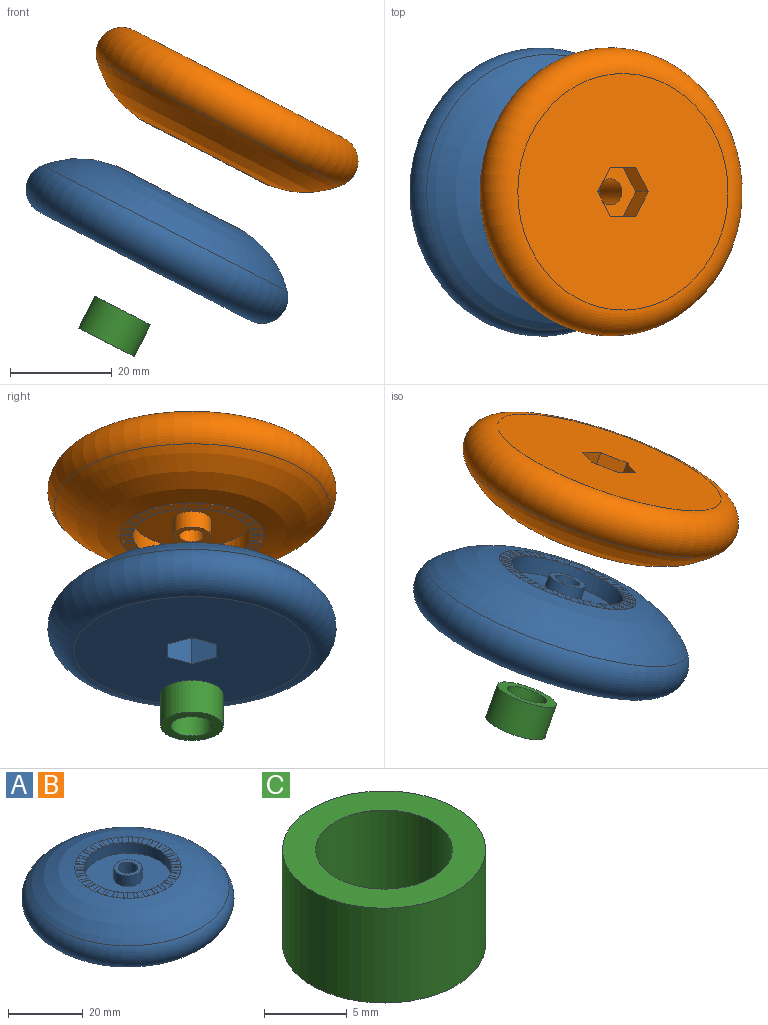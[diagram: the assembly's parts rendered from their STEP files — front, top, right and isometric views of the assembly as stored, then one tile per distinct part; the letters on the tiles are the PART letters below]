
ASSEMBLY  parts=3 mates=2
PART A: 166 faces, bbox 61.3x61.3x15 mm
  f0: plane 46.41x46.41mm, normal (0,0,-1), area 1611mm2, adj f7,f8,f9,f10,f11,f12,f13
  f1: plane 7.5x7.5mm, normal (0,0,1), area 23.7mm2, adj f6,f15
  f2: revolved ~53.87x53.87mm, area 3890.3mm2, adj f3,f7,f17,f22,f27,f32,f37,f42
  f3: plane 28.34x28.32mm, normal (0,0,1), area 130mm2, adj f2,f4,f16,f18,f19,f21,f23,f24
  f4: cylinder r=11.62mm len=23.25mm, axis (0,0,-1), area 255.6mm2, adj f3,f5
  f5: plane 23.25x23.25mm, normal (0,0,1), area 380.4mm2, adj f4,f6
  f6: cylinder r=3.75mm len=7.5mm, axis (0,0,-1), area 82.5mm2, adj f1,f5
  f7: torus R=23.21mm, axis (0,0,-1), area 1972.1mm2, adj f0,f2
  f8: plane 5.42x4.83mm, normal (-0.87,0.5,0), area 30.2mm2, adj f0,f9,f13,f14
  f9: plane 5.58x5.42mm, normal (0,1,0), area 30.2mm2, adj f0,f8,f10,f14
  f10: plane 5.42x4.83mm, normal (0.87,0.5,0), area 30.2mm2, adj f0,f9,f11,f14
  f11: plane 5.42x4.83mm, normal (0.87,-0.5,0), area 30.2mm2, adj f0,f10,f12,f14
  f12: plane 5.58x5.42mm, normal (0,-1,0), area 30.2mm2, adj f0,f11,f13,f14
  f13: plane 5.42x4.83mm, normal (-0.87,-0.5,0), area 30.2mm2, adj f0,f8,f12,f14
  f14: plane 11.16x9.66mm, normal (0,0,-1), area 60.4mm2, adj f8,f9,f10,f11,f12,f13,f15
  f15: cylinder r=2.55mm len=9.48mm, axis (0,0,1), area 152.1mm2, adj f1,f14
  f16: plane 2.52x0.1mm, normal (1,0,0), area 0.3mm2, adj f3,f17,f19,f20
  f17: plane 1.02x0.12mm, normal (0,1,0), area 0.1mm2, adj f2,f16,f18,f20
  f18: plane 2.52x0.1mm, normal (-1,0,0), area 0.3mm2, adj f3,f17,f19,f20
  f19: plane 1x0.1mm, normal (0,-1,0), area 0.1mm2, adj f3,f16,f18,f20
  f20: plane 2.52x1mm, normal (0,0,1), area 2.5mm2, adj f16,f17,f18,f19
  f21: plane 2.47x0.52mm, normal (0.98,-0.21,0), area 0.3mm2, adj f3,f22,f24,f25
  f22: plane 1x0.23mm, normal (0.21,0.98,0), area 0.1mm2, adj f2,f21,f23,f25
  f23: plane 2.47x0.52mm, normal (-0.98,0.21,0), area 0.3mm2, adj f3,f22,f24,f25
  f24: plane 0.98x0.21mm, normal (-0.21,-0.98,0), area 0.1mm2, adj f3,f21,f23,f25
  f25: plane 2.68x1.5mm, normal (0,0,1), area 2.5mm2, adj f21,f22,f23,f24
  f26: plane 2.3x1.03mm, normal (0.91,-0.41,0), area 0.3mm2, adj f3,f27,f29,f30
  f27: plane 0.93x0.42mm, normal (0.41,0.91,0), area 0.1mm2, adj f2,f26,f28,f30
  f28: plane 2.3x1.03mm, normal (-0.91,0.41,0), area 0.3mm2, adj f3,f27,f29,f30
  f29: plane 0.91x0.41mm, normal (-0.41,-0.91,0), area 0.1mm2, adj f3,f26,f28,f30
  f30: plane 2.71x1.94mm, normal (0,0,1), area 2.5mm2, adj f26,f27,f28,f29
  f31: plane 2.04x1.48mm, normal (0.81,-0.59,0), area 0.3mm2, adj f3,f32,f34,f35
  f32: plane 0.83x0.61mm, normal (0.59,0.81,0), area 0.1mm2, adj f2,f31,f33,f35
  f33: plane 2.04x1.48mm, normal (-0.81,0.59,0), area 0.3mm2, adj f3,f32,f34,f35
  f34: plane 0.81x0.59mm, normal (-0.59,-0.81,0), area 0.1mm2, adj f3,f31,f33,f35
  f35: plane 2.63x2.29mm, normal (0,0,1), area 2.5mm2, adj f31,f32,f33,f34
  f36: plane 1.88x1.69mm, normal (0.67,-0.74,0), area 0.3mm2, adj f3,f37,f39,f40
  f37: plane 0.76x0.69mm, normal (0.74,0.67,0), area 0.1mm2, adj f2,f36,f38,f40
  f38: plane 1.87x1.69mm, normal (-0.67,0.74,0), area 0.3mm2, adj f3,f37,f39,f40
  f39: plane 0.74x0.67mm, normal (-0.74,-0.67,0), area 0.1mm2, adj f3,f36,f38,f40
  f40: plane 2.54x2.43mm, normal (0,0,1), area 2.5mm2, adj f36,f37,f38,f39
  f41: plane 2.19x1.26mm, normal (0.5,-0.87,0), area 0.3mm2, adj f3,f42,f44,f45
  f42: plane 0.88x0.52mm, normal (0.87,0.5,0), area 0.1mm2, adj f2,f41,f43,f45
  f43: plane 2.19x1.26mm, normal (-0.5,0.87,0), area 0.3mm2, adj f3,f42,f44,f45
  f44: plane 0.87x0.5mm, normal (-0.87,-0.5,0), area 0.1mm2, adj f3,f41,f43,f45
  f45: plane 2.68x2.13mm, normal (0,0,1), area 2.5mm2, adj f41,f42,f43,f44
  f46: plane 2.4x0.78mm, normal (0.31,-0.95,0), area 0.3mm2, adj f3,f47,f49,f50
  f47: plane 0.97x0.33mm, normal (0.95,0.31,0), area 0.1mm2, adj f2,f46,f48,f50
  f48: plane 2.4x0.78mm, normal (-0.31,0.95,0), area 0.3mm2, adj f3,f47,f49,f50
  f49: plane 0.95x0.31mm, normal (-0.95,-0.31,0), area 0.1mm2, adj f3,f46,f48,f50
  f50: plane 2.71x1.73mm, normal (0,0,1), area 2.5mm2, adj f46,f47,f48,f49
  f51: plane 2.51x0.26mm, normal (0.1,-0.99,0), area 0.3mm2, adj f3,f52,f54,f55
  f52: plane 1.01x0.12mm, normal (0.99,0.1,0), area 0.1mm2, adj f2,f51,f53,f55
  f53: plane 2.51x0.26mm, normal (-0.1,0.99,0), area 0.3mm2, adj f3,f52,f54,f55
  f54: plane 0.99x0.1mm, normal (-0.99,-0.1,0), area 0.1mm2, adj f3,f51,f53,f55
  f55: plane 2.61x1.26mm, normal (0,0,1), area 2.5mm2, adj f51,f52,f53,f54
  f56: plane 2.51x0.26mm, normal (-0.1,-0.99,0), area 0.3mm2, adj f3,f57,f59,f60
  f57: plane 1.01x0.12mm, normal (0.99,-0.1,0), area 0.1mm2, adj f2,f56,f58,f60
  f58: plane 2.51x0.26mm, normal (0.1,0.99,0), area 0.3mm2, adj f3,f57,f59,f60
  f59: plane 0.99x0.1mm, normal (-0.99,0.1,0), area 0.1mm2, adj f3,f56,f58,f60
  f60: plane 2.61x1.26mm, normal (0,0,1), area 2.5mm2, adj f56,f57,f58,f59
  f61: plane 2.4x0.78mm, normal (-0.31,-0.95,0), area 0.3mm2, adj f3,f62,f64,f65
  f62: plane 0.97x0.33mm, normal (0.95,-0.31,0), area 0.1mm2, adj f2,f61,f63,f65
  f63: plane 2.4x0.78mm, normal (0.31,0.95,0), area 0.3mm2, adj f3,f62,f64,f65
  f64: plane 0.95x0.31mm, normal (-0.95,0.31,0), area 0.1mm2, adj f3,f61,f63,f65
  f65: plane 2.71x1.73mm, normal (0,0,1), area 2.5mm2, adj f61,f62,f63,f64
  f66: plane 2.19x1.26mm, normal (-0.5,-0.87,0), area 0.3mm2, adj f3,f67,f69,f70
  f67: plane 0.88x0.52mm, normal (0.87,-0.5,0), area 0.1mm2, adj f2,f66,f68,f70
  f68: plane 2.19x1.26mm, normal (0.5,0.87,0), area 0.3mm2, adj f3,f67,f69,f70
  f69: plane 0.87x0.5mm, normal (-0.87,0.5,0), area 0.1mm2, adj f3,f66,f68,f70
  f70: plane 2.68x2.13mm, normal (0,0,1), area 2.5mm2, adj f66,f67,f68,f69
  f71: plane 1.87x1.69mm, normal (-0.67,-0.74,0), area 0.3mm2, adj f3,f72,f74,f75
  f72: plane 0.76x0.69mm, normal (0.74,-0.67,0), area 0.1mm2, adj f2,f71,f73,f75
  f73: plane 1.88x1.69mm, normal (0.67,0.74,0), area 0.3mm2, adj f3,f72,f74,f75
  f74: plane 0.74x0.67mm, normal (-0.74,0.67,0), area 0.1mm2, adj f3,f71,f73,f75
  f75: plane 2.54x2.43mm, normal (0,0,1), area 2.5mm2, adj f71,f72,f73,f74
  f76: plane 2.04x1.48mm, normal (-0.81,-0.59,0), area 0.3mm2, adj f3,f77,f79,f80
  f77: plane 0.83x0.61mm, normal (0.59,-0.81,0), area 0.1mm2, adj f2,f76,f78,f80
  f78: plane 2.04x1.48mm, normal (0.81,0.59,0), area 0.3mm2, adj f3,f77,f79,f80
  f79: plane 0.81x0.59mm, normal (-0.59,0.81,0), area 0.1mm2, adj f3,f76,f78,f80
  f80: plane 2.63x2.29mm, normal (0,0,1), area 2.5mm2, adj f76,f77,f78,f79
  f81: plane 2.3x1.03mm, normal (-0.91,-0.41,0), area 0.3mm2, adj f3,f82,f84,f85
  f82: plane 0.93x0.42mm, normal (0.41,-0.91,0), area 0.1mm2, adj f2,f81,f83,f85
  f83: plane 2.3x1.03mm, normal (0.91,0.41,0), area 0.3mm2, adj f3,f82,f84,f85
  f84: plane 0.91x0.41mm, normal (-0.41,0.91,0), area 0.1mm2, adj f3,f81,f83,f85
  f85: plane 2.71x1.94mm, normal (0,0,1), area 2.5mm2, adj f81,f82,f83,f84
  f86: plane 2.47x0.52mm, normal (-0.98,-0.21,0), area 0.3mm2, adj f3,f87,f89,f90
  f87: plane 1x0.23mm, normal (0.21,-0.98,0), area 0.1mm2, adj f2,f86,f88,f90
  f88: plane 2.47x0.52mm, normal (0.98,0.21,0), area 0.3mm2, adj f3,f87,f89,f90
  f89: plane 0.98x0.21mm, normal (-0.21,0.98,0), area 0.1mm2, adj f3,f86,f88,f90
  f90: plane 2.68x1.5mm, normal (0,0,1), area 2.5mm2, adj f86,f87,f88,f89
  f91: plane 2.52x0.1mm, normal (-1,0,0), area 0.3mm2, adj f3,f92,f94,f95
  f92: plane 1.02x0.12mm, normal (0,-1,0), area 0.1mm2, adj f2,f91,f93,f95
  f93: plane 2.52x0.1mm, normal (1,0,0), area 0.3mm2, adj f3,f92,f94,f95
  f94: plane 1x0.1mm, normal (0,1,0), area 0.1mm2, adj f3,f91,f93,f95
  f95: plane 2.52x1mm, normal (0,0,1), area 2.5mm2, adj f91,f92,f93,f94
  f96: plane 2.47x0.52mm, normal (-0.98,0.21,0), area 0.3mm2, adj f3,f97,f99,f100
  f97: plane 1x0.23mm, normal (-0.21,-0.98,0), area 0.1mm2, adj f2,f96,f98,f100
  f98: plane 2.47x0.52mm, normal (0.98,-0.21,0), area 0.3mm2, adj f3,f97,f99,f100
  f99: plane 0.98x0.21mm, normal (0.21,0.98,0), area 0.1mm2, adj f3,f96,f98,f100
  f100: plane 2.68x1.5mm, normal (0,0,1), area 2.5mm2, adj f96,f97,f98,f99
  f101: plane 2.3x1.03mm, normal (-0.91,0.41,0), area 0.3mm2, adj f3,f102,f104,f105
  f102: plane 0.93x0.42mm, normal (-0.41,-0.91,0), area 0.1mm2, adj f2,f101,f103,f105
  f103: plane 2.3x1.03mm, normal (0.91,-0.41,0), area 0.3mm2, adj f3,f102,f104,f105
  f104: plane 0.91x0.41mm, normal (0.41,0.91,0), area 0.1mm2, adj f3,f101,f103,f105
  f105: plane 2.71x1.94mm, normal (0,0,1), area 2.5mm2, adj f101,f102,f103,f104
  f106: plane 2.04x1.48mm, normal (-0.81,0.59,0), area 0.3mm2, adj f3,f107,f109,f110
  f107: plane 0.83x0.61mm, normal (-0.59,-0.81,0), area 0.1mm2, adj f2,f106,f108,f110
  f108: plane 2.04x1.48mm, normal (0.81,-0.59,0), area 0.3mm2, adj f3,f107,f109,f110
  f109: plane 0.81x0.59mm, normal (0.59,0.81,0), area 0.1mm2, adj f3,f106,f108,f110
  f110: plane 2.63x2.29mm, normal (0,0,1), area 2.5mm2, adj f106,f107,f108,f109
  f111: plane 1.88x1.69mm, normal (-0.67,0.74,0), area 0.3mm2, adj f3,f112,f114,f115
  f112: plane 0.76x0.69mm, normal (-0.74,-0.67,0), area 0.1mm2, adj f2,f111,f113,f115
  f113: plane 1.87x1.69mm, normal (0.67,-0.74,0), area 0.3mm2, adj f3,f112,f114,f115
  f114: plane 0.74x0.67mm, normal (0.74,0.67,0), area 0.1mm2, adj f3,f111,f113,f115
  f115: plane 2.54x2.43mm, normal (0,0,1), area 2.5mm2, adj f111,f112,f113,f114
  f116: plane 2.19x1.26mm, normal (-0.5,0.87,0), area 0.3mm2, adj f3,f117,f119,f120
  f117: plane 0.88x0.52mm, normal (-0.87,-0.5,0), area 0.1mm2, adj f2,f116,f118,f120
  f118: plane 2.19x1.26mm, normal (0.5,-0.87,0), area 0.3mm2, adj f3,f117,f119,f120
  f119: plane 0.87x0.5mm, normal (0.87,0.5,0), area 0.1mm2, adj f3,f116,f118,f120
  f120: plane 2.68x2.13mm, normal (0,0,1), area 2.5mm2, adj f116,f117,f118,f119
  f121: plane 2.4x0.78mm, normal (-0.31,0.95,0), area 0.3mm2, adj f3,f122,f124,f125
  f122: plane 0.97x0.33mm, normal (-0.95,-0.31,0), area 0.1mm2, adj f2,f121,f123,f125
  f123: plane 2.4x0.78mm, normal (0.31,-0.95,0), area 0.3mm2, adj f3,f122,f124,f125
  f124: plane 0.95x0.31mm, normal (0.95,0.31,0), area 0.1mm2, adj f3,f121,f123,f125
  f125: plane 2.71x1.73mm, normal (0,0,1), area 2.5mm2, adj f121,f122,f123,f124
  f126: plane 2.51x0.26mm, normal (-0.1,0.99,0), area 0.3mm2, adj f3,f127,f129,f130
  f127: plane 1.01x0.12mm, normal (-0.99,-0.1,0), area 0.1mm2, adj f2,f126,f128,f130
  f128: plane 2.51x0.26mm, normal (0.1,-0.99,0), area 0.3mm2, adj f3,f127,f129,f130
  f129: plane 0.99x0.1mm, normal (0.99,0.1,0), area 0.1mm2, adj f3,f126,f128,f130
  f130: plane 2.61x1.26mm, normal (0,0,1), area 2.5mm2, adj f126,f127,f128,f129
  f131: plane 2.51x0.26mm, normal (0.1,0.99,0), area 0.3mm2, adj f3,f132,f134,f135
  f132: plane 1.01x0.12mm, normal (-0.99,0.1,0), area 0.1mm2, adj f2,f131,f133,f135
  f133: plane 2.51x0.26mm, normal (-0.1,-0.99,0), area 0.3mm2, adj f3,f132,f134,f135
  f134: plane 0.99x0.1mm, normal (0.99,-0.1,0), area 0.1mm2, adj f3,f131,f133,f135
  f135: plane 2.61x1.26mm, normal (0,0,1), area 2.5mm2, adj f131,f132,f133,f134
  f136: plane 2.4x0.78mm, normal (0.31,0.95,0), area 0.3mm2, adj f3,f137,f139,f140
  f137: plane 0.97x0.33mm, normal (-0.95,0.31,0), area 0.1mm2, adj f2,f136,f138,f140
  f138: plane 2.4x0.78mm, normal (-0.31,-0.95,0), area 0.3mm2, adj f3,f137,f139,f140
  f139: plane 0.95x0.31mm, normal (0.95,-0.31,0), area 0.1mm2, adj f3,f136,f138,f140
  f140: plane 2.71x1.73mm, normal (0,0,1), area 2.5mm2, adj f136,f137,f138,f139
  f141: plane 2.19x1.26mm, normal (0.5,0.87,0), area 0.3mm2, adj f3,f142,f144,f145
  f142: plane 0.88x0.52mm, normal (-0.87,0.5,0), area 0.1mm2, adj f2,f141,f143,f145
  f143: plane 2.19x1.26mm, normal (-0.5,-0.87,0), area 0.3mm2, adj f3,f142,f144,f145
  f144: plane 0.87x0.5mm, normal (0.87,-0.5,0), area 0.1mm2, adj f3,f141,f143,f145
  f145: plane 2.68x2.13mm, normal (0,0,1), area 2.5mm2, adj f141,f142,f143,f144
  f146: plane 1.87x1.69mm, normal (0.67,0.74,0), area 0.3mm2, adj f3,f147,f149,f150
  f147: plane 0.76x0.69mm, normal (-0.74,0.67,0), area 0.1mm2, adj f2,f146,f148,f150
  f148: plane 1.88x1.69mm, normal (-0.67,-0.74,0), area 0.3mm2, adj f3,f147,f149,f150
  f149: plane 0.74x0.67mm, normal (0.74,-0.67,0), area 0.1mm2, adj f3,f146,f148,f150
  f150: plane 2.54x2.43mm, normal (0,0,1), area 2.5mm2, adj f146,f147,f148,f149
  f151: plane 2.04x1.48mm, normal (0.81,0.59,0), area 0.3mm2, adj f3,f152,f154,f155
  f152: plane 0.83x0.61mm, normal (-0.59,0.81,0), area 0.1mm2, adj f2,f151,f153,f155
  f153: plane 2.04x1.48mm, normal (-0.81,-0.59,0), area 0.3mm2, adj f3,f152,f154,f155
  f154: plane 0.81x0.59mm, normal (0.59,-0.81,0), area 0.1mm2, adj f3,f151,f153,f155
  f155: plane 2.63x2.29mm, normal (0,0,1), area 2.5mm2, adj f151,f152,f153,f154
  f156: plane 2.3x1.03mm, normal (0.91,0.41,0), area 0.3mm2, adj f3,f157,f159,f160
  f157: plane 0.93x0.42mm, normal (-0.41,0.91,0), area 0.1mm2, adj f2,f156,f158,f160
  f158: plane 2.3x1.03mm, normal (-0.91,-0.41,0), area 0.3mm2, adj f3,f157,f159,f160
  f159: plane 0.91x0.41mm, normal (0.41,-0.91,0), area 0.1mm2, adj f3,f156,f158,f160
  f160: plane 2.71x1.94mm, normal (0,0,1), area 2.5mm2, adj f156,f157,f158,f159
  f161: plane 2.47x0.52mm, normal (0.98,0.21,0), area 0.3mm2, adj f3,f162,f164,f165
  f162: plane 1x0.23mm, normal (-0.21,0.98,0), area 0.1mm2, adj f2,f161,f163,f165
  f163: plane 2.47x0.52mm, normal (-0.98,-0.21,0), area 0.3mm2, adj f3,f162,f164,f165
  f164: plane 0.98x0.21mm, normal (0.21,-0.98,0), area 0.1mm2, adj f3,f161,f163,f165
  f165: plane 2.68x1.5mm, normal (0,0,1), area 2.5mm2, adj f161,f162,f163,f164
PART B: same geometry as A
PART C: 4 faces, bbox 12.3x12.3x7 mm
  f0: cylinder r=4.13mm len=8.26mm, axis (0,0,-1), area 181.5mm2, adj f2,f3
  f1: cylinder r=6.13mm len=12.26mm, axis (0,0,-1), area 269.5mm2, adj f2,f3
  f2: plane 12.26x12.26mm, normal (0,0,1), area 64.4mm2, adj f0,f1
  f3: plane 12.26x12.26mm, normal (0,0,-1), area 64.4mm2, adj f0,f1
PLACE A rot(axis=(0,1,0),27.2deg) t=(-35.2,-21.37,-30.95)mm
PLACE B rot(axis=(-0.97,0,0.24),180deg) t=(-16.81,-21.37,4.83)mm
PLACE C rot(axis=(0,1,0),27.2deg) t=(-42.82,-21.37,-45.78)mm
MATE cylindrical B.f4 <-> C.f0  axis (0.46,0,0.89) through (-22.82,-21.37,-6.87)mm
MATE cylindrical A.f4 <-> C.f0  axis (-0.46,0,-0.89) through (-29.19,-21.37,-19.25)mm
